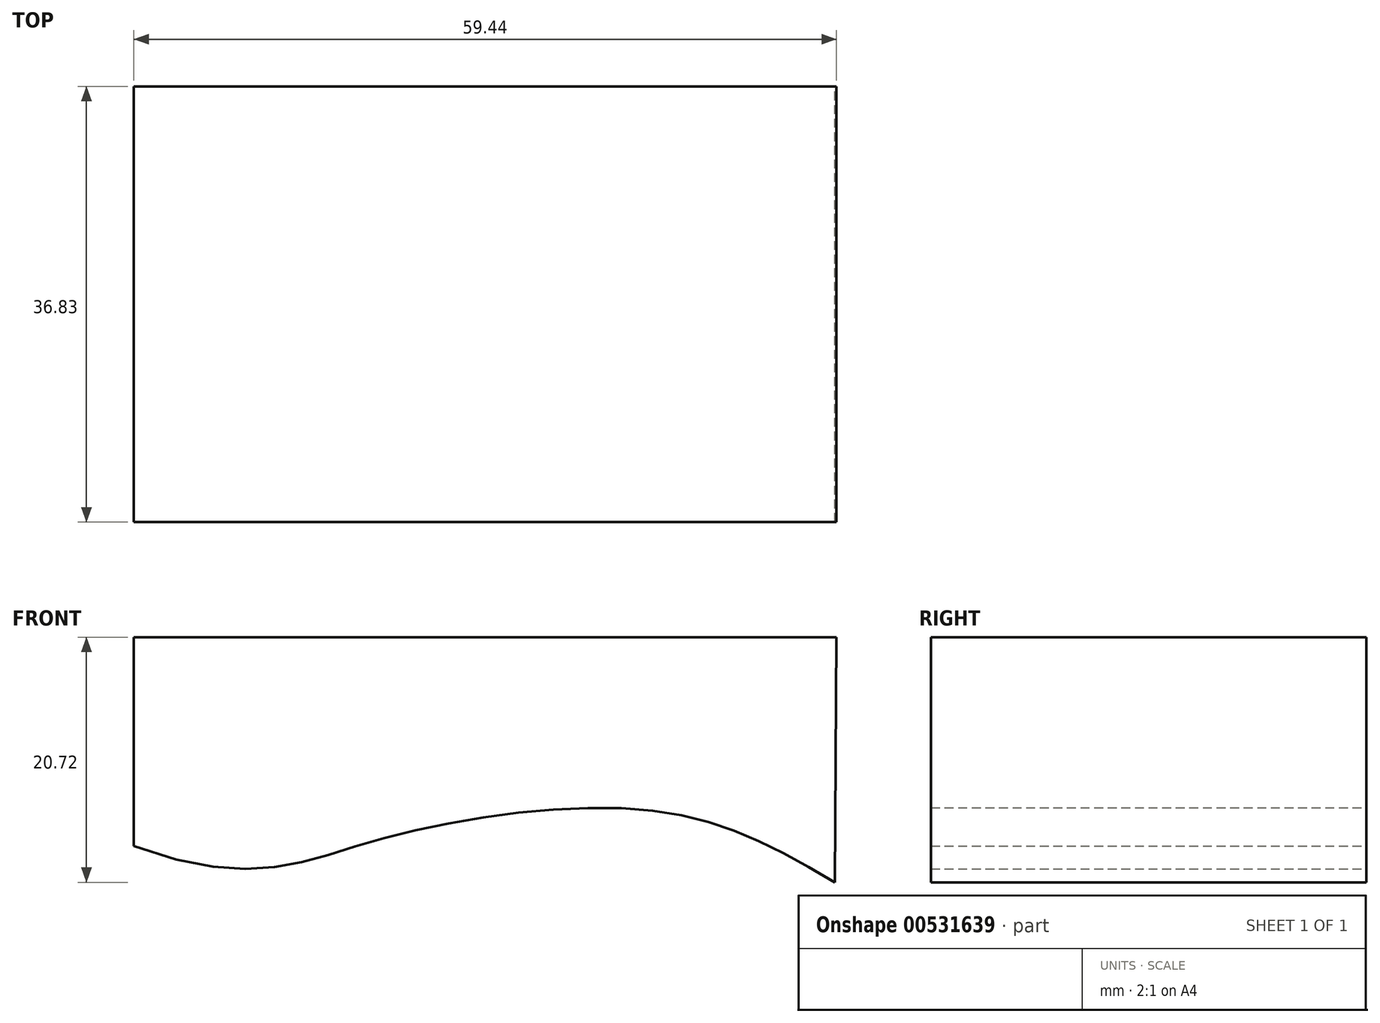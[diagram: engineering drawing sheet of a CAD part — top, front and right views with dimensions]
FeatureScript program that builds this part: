
annotation { "Feature Type Name" : "Feature", "Feature Type Description" : "" }
export const myFeature = defineFeature(function(context is Context, id is Id, definition is map)
    precondition{}
    {
        {
            var Q0;
            Q0=qCreatedBy(makeId("Front.planeOp"),FACE);
            var sketch = newSketch(context, id + "F0", { "sketchPlane" : qUnion([Q0])});
            skFitSpline(sketch, "E0", {"points": [v(-22.58, -10.95) * mm, v(-2, -10.43) * mm, v(21.48, -7.96) * mm, v(36.72, -14) * mm], "startDerivative": vector(88.52, -32.51) * mm, "endDerivative": vector(52.83, -30.94) * mm});
            skLineSegment(sketch, "E1", {"start": v(-22.58, -10.95) * mm, "end": v(-22.58, 6.72) * mm});
            skLineSegment(sketch, "E2", {"start": v(-22.58, 6.72) * mm, "end": v(36.86, 6.72) * mm});
            skLineSegment(sketch, "E3", {"start": v(36.86, 6.72) * mm, "end": v(36.72, -14) * mm});
            skSolve(sketch);
        }
        {
            var Q0;
            Q0=makeQuery(id+"F0.imprint","IMPRINT",FACE,{"disambiguationData":[TD([[makeQuery(id+"F0.imprint","IMPRINT",EDGE,{"derivedFrom":sQuery(id+"F0.wireOp",EDGE,"E0")}),1.0]])]});
            var Q1;
            Q1 = qSketchRegion(id + "F0", true);
            extrude(context, id + "F1", {"entities" : qUnion([Q0, Q1]), "depth" : 36.83 * mm, "offsetDistance" : 25.4 * mm});
        }
    });
